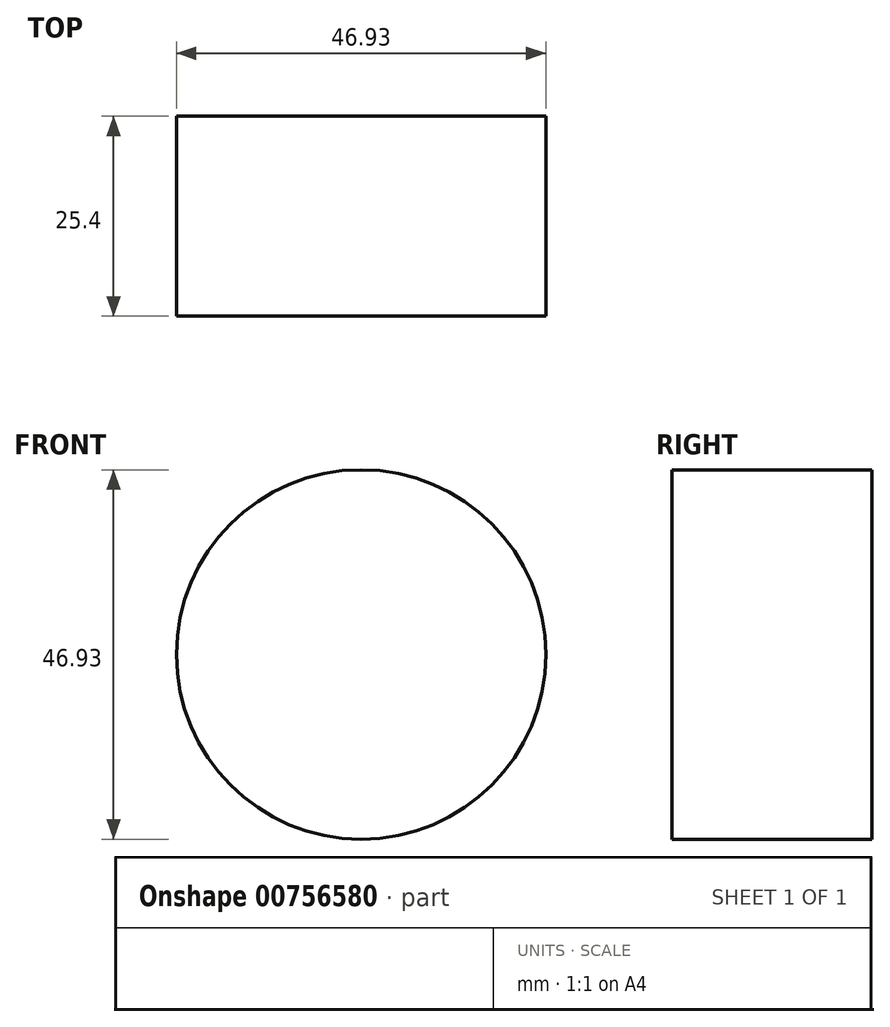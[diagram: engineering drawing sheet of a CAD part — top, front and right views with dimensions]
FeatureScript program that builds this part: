
annotation { "Feature Type Name" : "Feature", "Feature Type Description" : "" }
export const myFeature = defineFeature(function(context is Context, id is Id, definition is map)
    precondition{}
    {
        {
            var Q0;
            Q0=qCreatedBy(makeId("Front.planeOp"),FACE);
            var sketch = newSketch(context, id + "F0", { "sketchPlane" : qUnion([Q0])});
            skCircle(sketch, "E0", {"center": v(42.57, 46.98) * mm, "radius": 23.47 * mm});
            skSolve(sketch);
        }
        {
            var Q0;
            Q0 = qSketchRegion(id + "F0", true);
            extrude(context, id + "F1", {"entities" : qUnion([Q0]), "depth" : 25.4 * mm, "offsetDistance" : 25.4 * mm});
        }
    });
